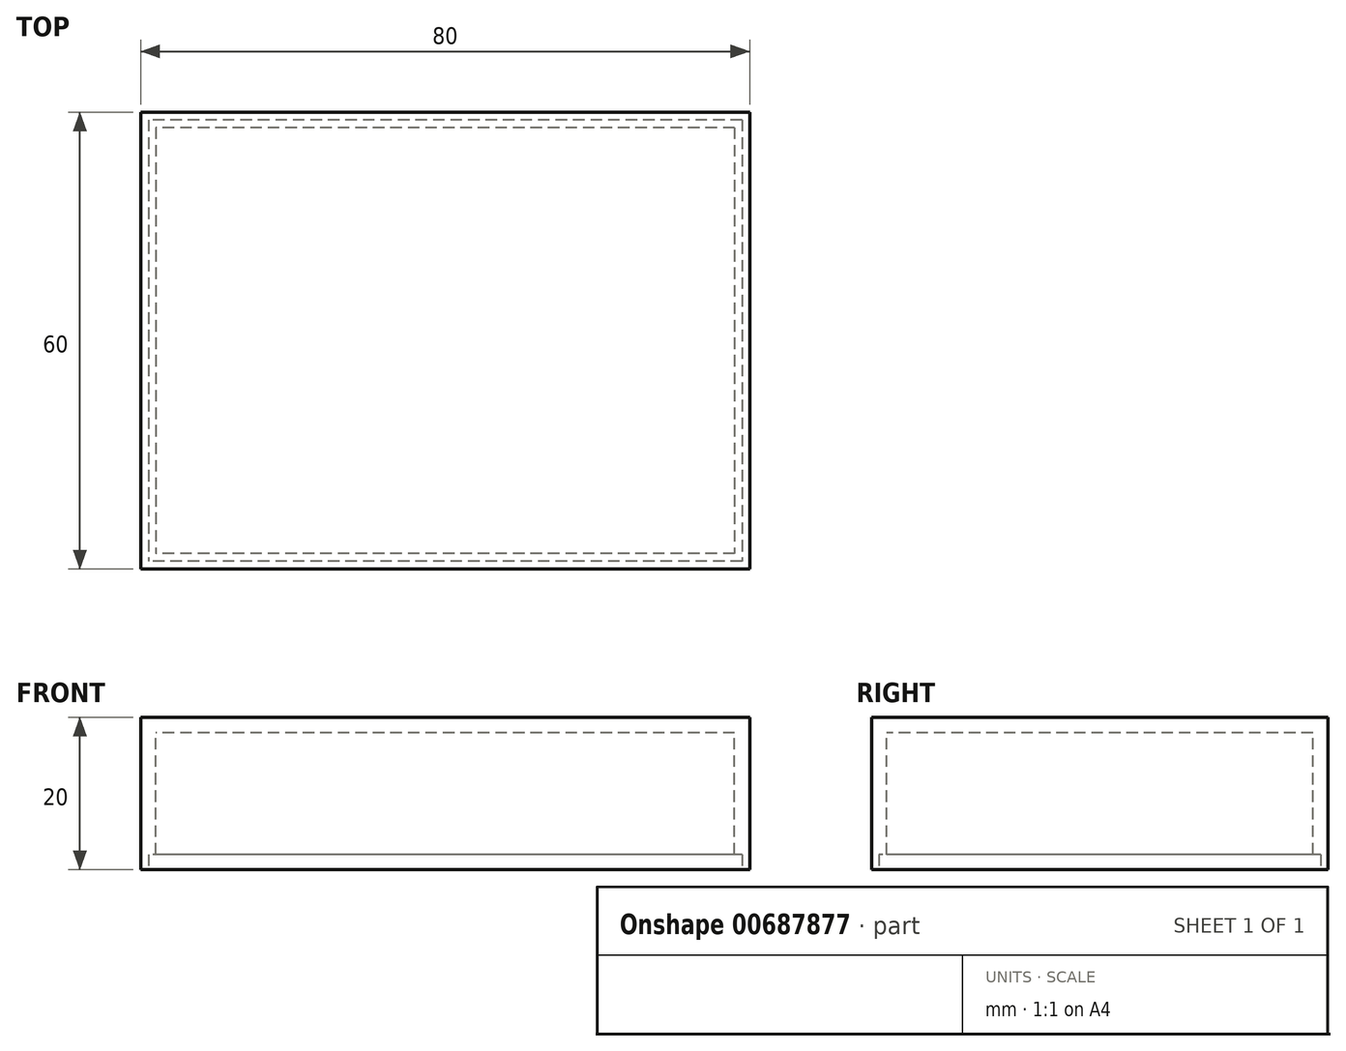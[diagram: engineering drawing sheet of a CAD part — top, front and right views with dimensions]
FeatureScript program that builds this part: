
annotation { "Feature Type Name" : "Feature", "Feature Type Description" : "" }
export const myFeature = defineFeature(function(context is Context, id is Id, definition is map)
    precondition{}
    {
        {
            var Q0;
            Q0=qCreatedBy(makeId("Top.planeOp"),FACE);
            var sketch = newSketch(context, id + "F0", { "sketchPlane" : qUnion([Q0])});
            skLineSegment(sketch, "E0.bottom", {"start": v(40, 30) * mm, "end": v(-40, 30) * mm});
            skLineSegment(sketch, "E0.top", {"start": v(40, -30) * mm, "end": v(-40, -30) * mm});
            skLineSegment(sketch, "E0.left", {"start": v(40, 30) * mm, "end": v(40, -30) * mm});
            skLineSegment(sketch, "E0.right", {"start": v(-40, 30) * mm, "end": v(-40, -30) * mm});
            skPoint(sketch, "E0.middle", {"position": v(0, 0) * mm});
            skSolve(sketch);
        }
        {
            var Q0;
            Q0=makeQuery(id+"F0.imprint","IMPRINT",FACE,{"disambiguationData":[TD([[makeQuery(id+"F0.imprint","IMPRINT",EDGE,{"derivedFrom":sQuery(id+"F0.wireOp",EDGE,"E0.bottom")}),1.0]])]});
            extrude(context, id + "F1", {"entities" : qUnion([Q0]), "oppositeDirection" : true, "depth" : 20 * mm, "offsetDistance" : 25 * mm});
        }
        {
            var Q0;
            Q0=makeQuery(id+"F1.opExtrude","CAP_FACE",FACE,{"disambiguationData":[OSD([sQuery(id+"F0.wireOp",EDGE,"E0.bottom"),sQuery(id+"F0.wireOp",EDGE,"E0.top"),sQuery(id+"F0.wireOp",EDGE,"E0.left"),sQuery(id+"F0.wireOp",EDGE,"E0.right")])],"isStart":false});
            shell(context, id + "F2", {"entities" : qUnion([Q0]), "thickness" : 2 * mm});
        }
        {
            var Q0;
            Q0=makeQuery(id+"F1.opExtrude","CAP_FACE",FACE,{"disambiguationData":[OSD([sQuery(id+"F0.wireOp",EDGE,"E0.bottom"),sQuery(id+"F0.wireOp",EDGE,"E0.top"),sQuery(id+"F0.wireOp",EDGE,"E0.left"),sQuery(id+"F0.wireOp",EDGE,"E0.right")])],"isStart":false});
            var sketch = newSketch(context, id + "F3", { "sketchPlane" : qUnion([Q0])});
            skLineSegment(sketch, "E1.0", {"start": v(39, 29) * mm, "end": v(-39, 29) * mm});
            skLineSegment(sketch, "E1.1", {"start": v(39, -29) * mm, "end": v(39, 29) * mm});
            skLineSegment(sketch, "E1.2", {"start": v(39, -29) * mm, "end": v(-39, -29) * mm});
            skLineSegment(sketch, "E1.3", {"start": v(-39, -29) * mm, "end": v(-39, 29) * mm});
            skSolve(sketch);
        }
        {
            var Q0;
            Q0 = qSketchRegion(id + "F3", true);
            extrude(context, id + "F4", {"entities" : qUnion([Q0]), "operationType" : NewBodyOperationType.REMOVE, "oppositeDirection" : true, "depth" : 2 * mm, "offsetDistance" : 25 * mm});
        }
    });
